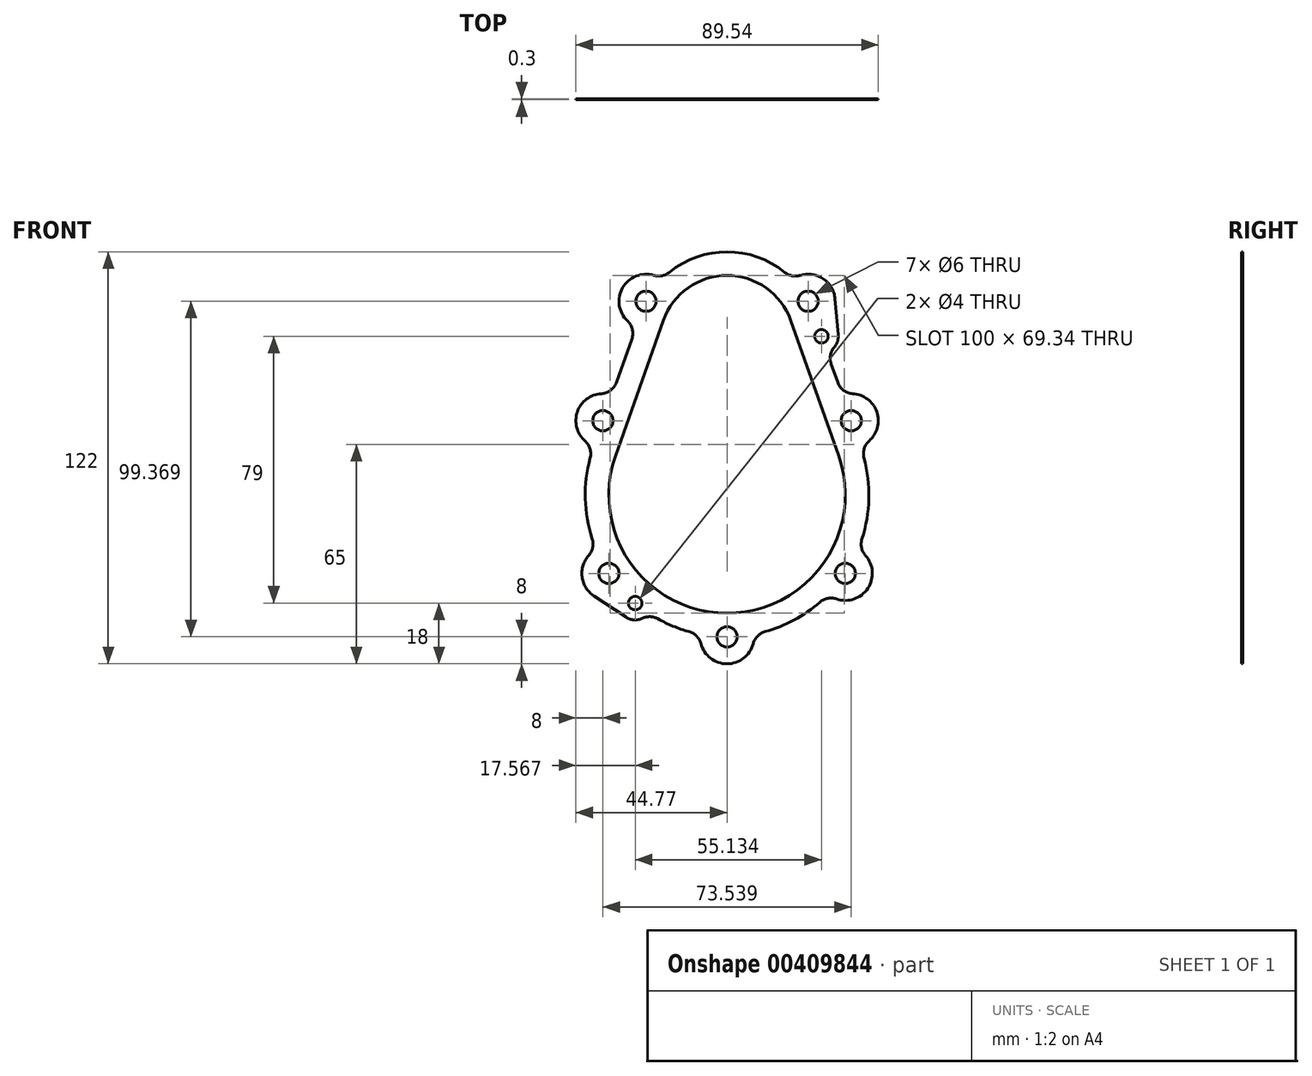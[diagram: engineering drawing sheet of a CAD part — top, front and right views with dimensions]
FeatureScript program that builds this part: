
annotation { "Feature Type Name" : "Feature", "Feature Type Description" : "" }
export const myFeature = defineFeature(function(context is Context, id is Id, definition is map)
    precondition{}
    {
        {
            var Q0;
            Q0=qCreatedBy(makeId("Front.planeOp"),FACE);
            var sketch = newSketch(context, id + "F0", { "sketchPlane" : qUnion([Q0])});
            skArc(sketch, "E0.0.0", {"start": v(17.06, 20.93) * mm, "mid": v(0, 27) * mm, "end": v(-17.06, 20.93) * mm});
            skArc(sketch, "E0.0.1", {"start": v(-17.06, 20.93) * mm, "mid": v(-19.25, 19.9) * mm, "end": v(-21.67, 20.02) * mm});
            skArc(sketch, "E0.0.2", {"start": v(-21.67, 20.02) * mm, "mid": v(-30.92, 16.38) * mm, "end": v(-29.49, 6.55) * mm});
            skArc(sketch, "E0.0.3", {"start": v(-29.49, 6.55) * mm, "mid": v(-28.05, 4.08) * mm, "end": v(-28.2, 1.24) * mm});
            skLineSegment(sketch, "E0.0.4", {"start": v(-28.2, 1.24) * mm, "end": v(-32.77, -11.69) * mm});
            skArc(sketch, "E0.0.5", {"start": v(-32.77, -11.69) * mm, "mid": v(-34.49, -14.02) * mm, "end": v(-37.2, -15.01) * mm});
            skArc(sketch, "E0.0.6", {"start": v(-37.2, -15.01) * mm, "mid": v(-44.33, -20.38) * mm, "end": v(-42.06, -29) * mm});
            skArc(sketch, "E0.0.7", {"start": v(-42.06, -29) * mm, "mid": v(-40.59, -31.3) * mm, "end": v(-40.55, -34.05) * mm});
            skArc(sketch, "E0.0.8", {"start": v(-40.55, -34.05) * mm, "mid": v(-41.99, -46.07) * mm, "end": v(-39.94, -58) * mm});
            skArc(sketch, "E0.0.9", {"start": v(-39.94, -58) * mm, "mid": v(-39.8, -60.58) * mm, "end": v(-40.96, -62.88) * mm});
            skArc(sketch, "E0.0.10", {"start": v(-40.96, -62.88) * mm, "mid": v(-42.94, -69.23) * mm, "end": v(-39.43, -74.88) * mm});
            skLineSegment(sketch, "E0.0.11", {"start": v(-39.43, -74.88) * mm, "end": v(-29.97, -81.16) * mm});
            skArc(sketch, "E0.0.12", {"start": v(-29.97, -81.16) * mm, "mid": v(-27.56, -81.99) * mm, "end": v(-25.06, -81.52) * mm});
            skArc(sketch, "E0.0.13", {"start": v(-25.06, -81.52) * mm, "mid": v(-22.75, -81.04) * mm, "end": v(-20.48, -81.67) * mm});
            skArc(sketch, "E0.0.14", {"start": v(-20.48, -81.67) * mm, "mid": v(-15.97, -83.84) * mm, "end": v(-11.24, -85.47) * mm});
            skArc(sketch, "E0.0.15", {"start": v(-11.24, -85.47) * mm, "mid": v(-9.02, -86.78) * mm, "end": v(-7.74, -89.02) * mm});
            skArc(sketch, "E0.0.16", {"start": v(-7.74, -89.02) * mm, "mid": v(0, -95) * mm, "end": v(7.74, -89.02) * mm});
            skArc(sketch, "E0.0.17", {"start": v(7.74, -89.02) * mm, "mid": v(9.02, -86.78) * mm, "end": v(11.24, -85.47) * mm});
            skArc(sketch, "E0.0.18", {"start": v(11.24, -85.47) * mm, "mid": v(19.86, -82) * mm, "end": v(27.51, -76.74) * mm});
            skArc(sketch, "E0.0.19", {"start": v(27.51, -76.74) * mm, "mid": v(29.83, -75.6) * mm, "end": v(32.4, -75.78) * mm});
            skArc(sketch, "E0.0.20", {"start": v(32.4, -75.78) * mm, "mid": v(41.67, -72.64) * mm, "end": v(40.96, -62.88) * mm});
            skArc(sketch, "E0.0.21", {"start": v(40.96, -62.88) * mm, "mid": v(39.8, -60.58) * mm, "end": v(39.94, -58) * mm});
            skArc(sketch, "E0.0.22", {"start": v(39.94, -58) * mm, "mid": v(41.99, -46.07) * mm, "end": v(40.55, -34.05) * mm});
            skArc(sketch, "E0.0.23", {"start": v(40.55, -34.05) * mm, "mid": v(40.59, -31.3) * mm, "end": v(42.06, -29) * mm});
            skArc(sketch, "E0.0.24", {"start": v(42.06, -29) * mm, "mid": v(44.33, -20.38) * mm, "end": v(37.2, -15.01) * mm});
            skArc(sketch, "E0.0.25", {"start": v(37.2, -15.01) * mm, "mid": v(34.49, -14.02) * mm, "end": v(32.77, -11.69) * mm});
            skLineSegment(sketch, "E0.0.26", {"start": v(32.77, -11.69) * mm, "end": v(30.82, -6.16) * mm});
            skArc(sketch, "E0.0.27", {"start": v(30.82, -6.16) * mm, "mid": v(30.62, -3.58) * mm, "end": v(31.73, -1.25) * mm});
            skArc(sketch, "E0.0.28", {"start": v(31.73, -1.25) * mm, "mid": v(32.7, 0.48) * mm, "end": v(32.91, 2.44) * mm});
            skLineSegment(sketch, "E0.0.29", {"start": v(32.91, 2.44) * mm, "end": v(31.97, 13.08) * mm});
            skArc(sketch, "E0.0.30", {"start": v(31.97, 13.08) * mm, "mid": v(28.47, 19) * mm, "end": v(21.67, 20.02) * mm});
            skArc(sketch, "E0.0.31", {"start": v(21.67, 20.02) * mm, "mid": v(19.25, 19.9) * mm, "end": v(17.06, 20.93) * mm});
            skCircle(sketch, "E1.0", {"center": v(-24, 12.37) * mm, "radius": 3 * mm});
            skCircle(sketch, "E2.0", {"center": v(-36.77, -23) * mm, "radius": 3 * mm});
            skCircle(sketch, "E3.0", {"center": v(-35, -68.22) * mm, "radius": 3 * mm});
            skCircle(sketch, "E4.0", {"center": v(-27.2, -77) * mm, "radius": 2 * mm});
            skCircle(sketch, "E5.0", {"center": v(0, -87) * mm, "radius": 3 * mm});
            skCircle(sketch, "E6.0", {"center": v(35, -68.22) * mm, "radius": 3 * mm});
            skCircle(sketch, "E7.0", {"center": v(36.77, -23) * mm, "radius": 3 * mm});
            skCircle(sketch, "E8.0", {"center": v(27.93, 2) * mm, "radius": 2 * mm});
            skCircle(sketch, "E9.0", {"center": v(24, 12.37) * mm, "radius": 3 * mm});
            skLineSegment(sketch, "E10.0", {"start": v(-18.86, 6.67) * mm, "end": v(-33, -33.33) * mm});
            skArc(sketch, "E11.0", {"start": v(18.86, 6.67) * mm, "mid": v(0, 20) * mm, "end": v(-18.86, 6.67) * mm});
            skPoint(sketch, "E12.0", {"position": v(25.93, -13.33) * mm});
            skArc(sketch, "E13.0", {"start": v(-33, -33.33) * mm, "mid": v(0, -80) * mm, "end": v(33, -33.33) * mm});
            skLineSegment(sketch, "E14.0", {"start": v(33, -33.33) * mm, "end": v(18.86, 6.67) * mm});
            skSolve(sketch);
        }
        {
            var Q0;
            Q0 = qSketchRegion(id + "F0", true);
            extrude(context, id + "F1", {"entities" : qUnion([Q0]), "depth" : 0.3 * mm});
        }
    });
